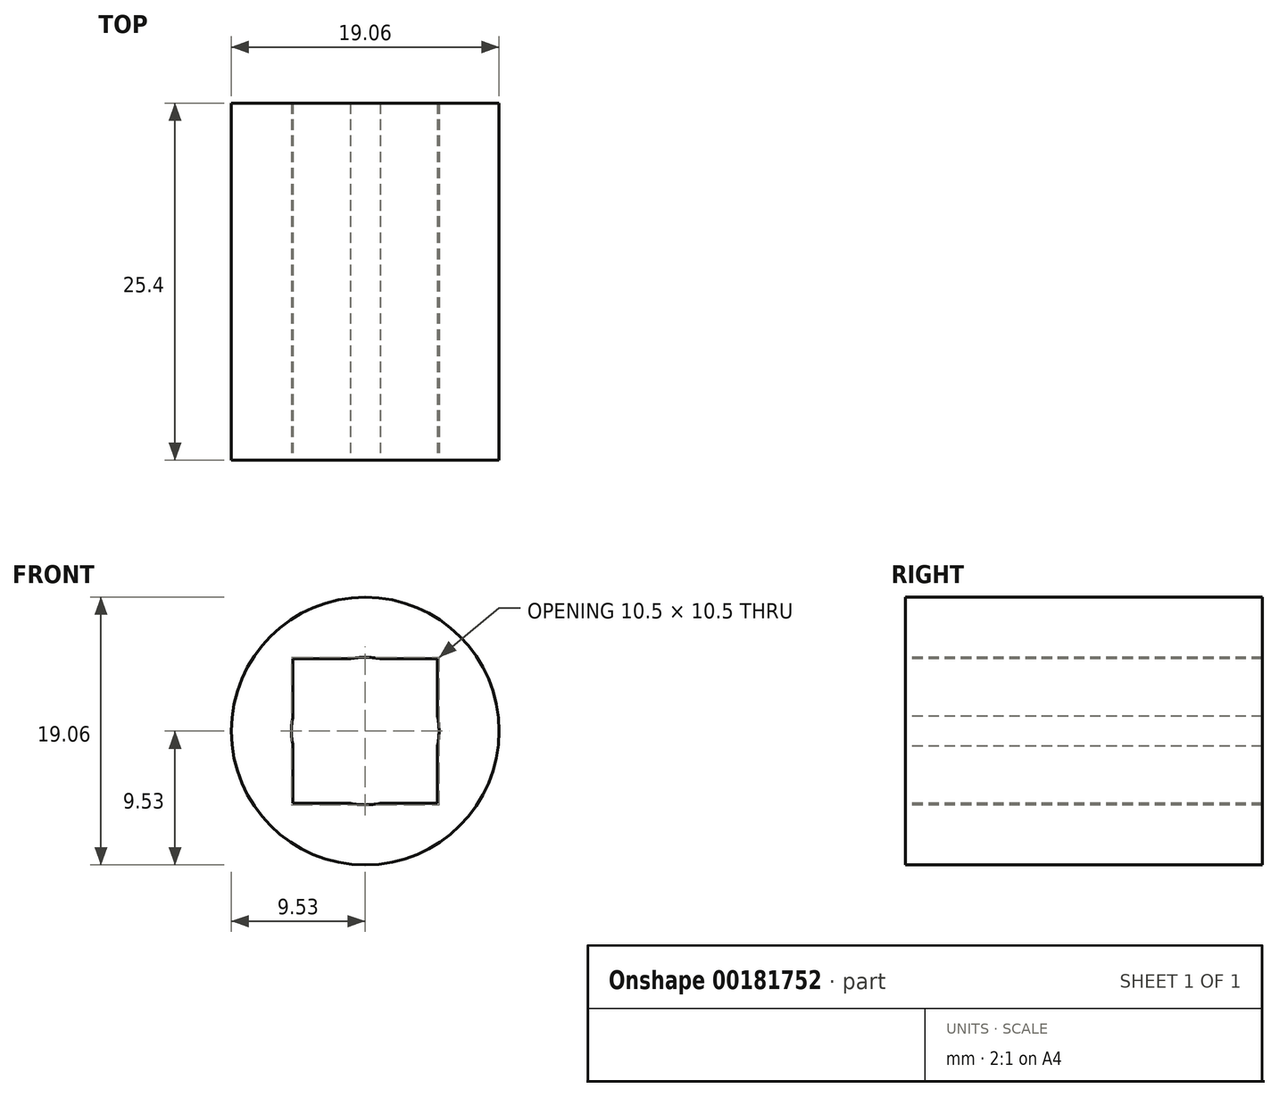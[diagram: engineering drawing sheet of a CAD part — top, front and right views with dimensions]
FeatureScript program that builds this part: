
annotation { "Feature Type Name" : "Feature", "Feature Type Description" : "" }
export const myFeature = defineFeature(function(context is Context, id is Id, definition is map)
    precondition{}
    {
        {
            var Q0;
            Q0=qCreatedBy(makeId("Front.planeOp"),FACE);
            var sketch = newSketch(context, id + "F0", { "sketchPlane" : qUnion([Q0])});
            skCircle(sketch, "E0", {"center": v(0, 0) * mm, "radius": 9.53 * mm});
            skSolve(sketch);
        }
        {
            var Q0;
            Q0=makeQuery(id+"F0.imprint","IMPRINT",FACE,{"disambiguationData":[TD([[makeQuery(id+"F0.imprint","IMPRINT",EDGE,{"derivedFrom":sQuery(id+"F0.wireOp",EDGE,"E0")}),1.0]])]});
            extrude(context, id + "F1", {"entities" : qUnion([Q0]), "depth" : 25.4 * mm});
        }
        {
            var Q0;
            Q0=qCreatedBy(makeId("Front.planeOp"),FACE);
            var sketch = newSketch(context, id + "F2", { "sketchPlane" : qUnion([Q0])});
            skLineSegment(sketch, "E1.bottom", {"start": v(-5.14, 5.14) * mm, "end": v(5.14, 5.14) * mm});
            skLineSegment(sketch, "E1.top", {"start": v(-5.14, -5.14) * mm, "end": v(5.14, -5.14) * mm});
            skLineSegment(sketch, "E1.left", {"start": v(-5.14, 5.14) * mm, "end": v(-5.14, -5.14) * mm});
            skLineSegment(sketch, "E1.right", {"start": v(5.14, 5.14) * mm, "end": v(5.14, -5.14) * mm});
            skPoint(sketch, "E1.middle", {"position": v(0, 0) * mm});
            skCircle(sketch, "E2", {"center": v(0, 0) * mm, "radius": 5.25 * mm});
            skSolve(sketch);
        }
        {
            var Q0;
            Q0 = qSketchRegion(id + "F2", true);
            extrude(context, id + "F3", {"entities" : qUnion([Q0]), "operationType" : NewBodyOperationType.REMOVE, "oppositeDirection" : true, "depth" : 25.4 * mm, "hasSecondDirection" : true, "secondDirectionOppositeDirection" : false, "secondDirectionDepth" : 25.4 * mm});
        }
    });
